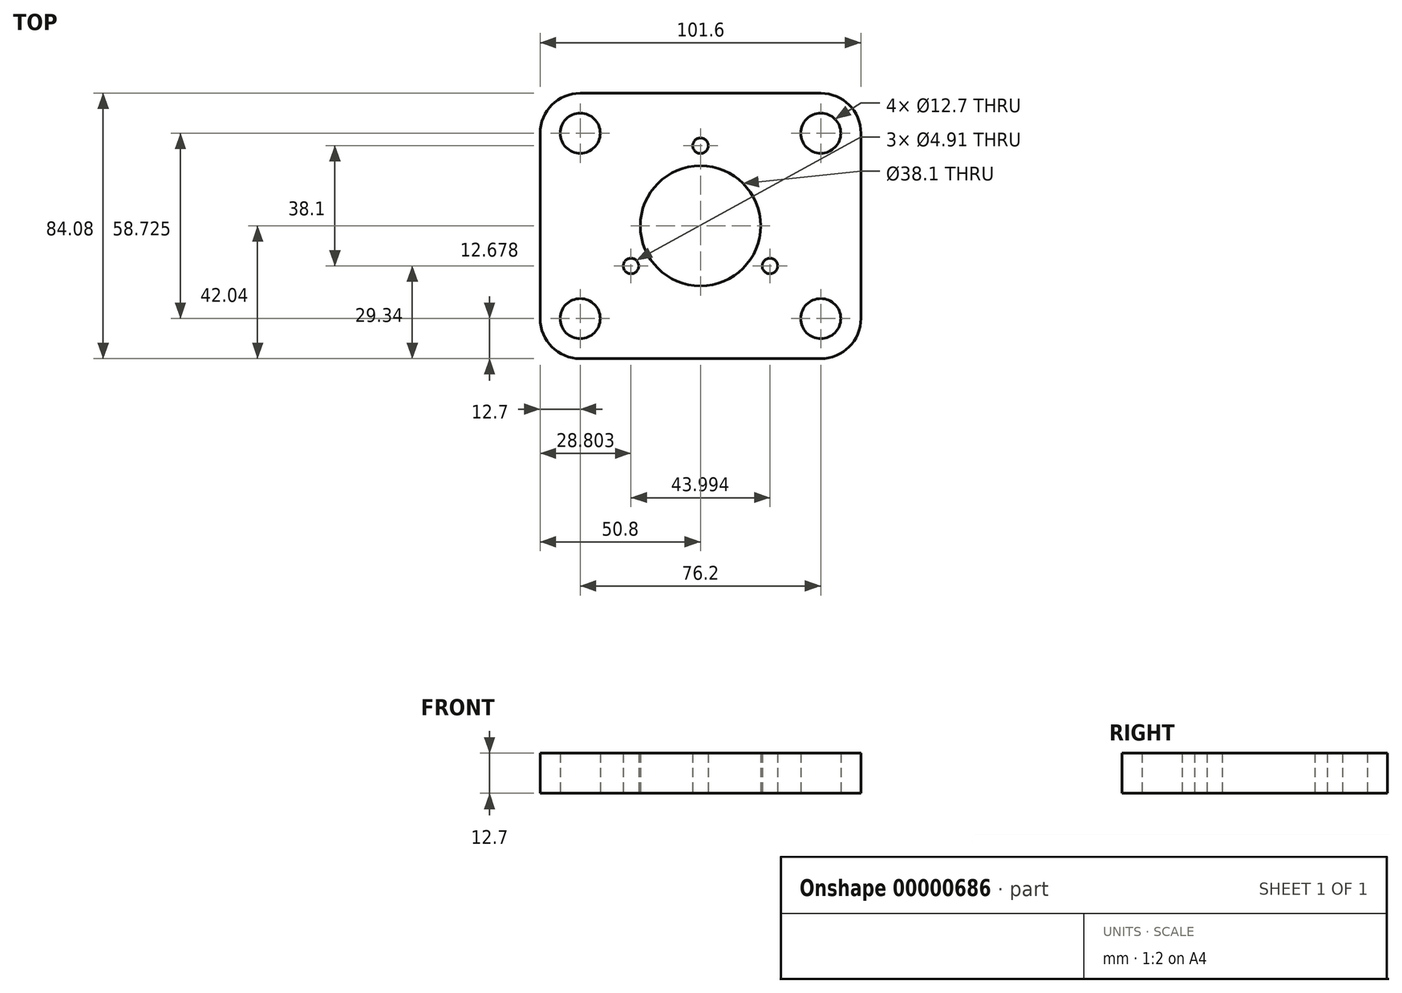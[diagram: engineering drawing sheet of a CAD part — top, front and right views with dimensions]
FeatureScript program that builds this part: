
annotation { "Feature Type Name" : "Feature", "Feature Type Description" : "" }
export const myFeature = defineFeature(function(context is Context, id is Id, definition is map)
    precondition{}
    {
        {
            var Q0;
            Q0=qCreatedBy(makeId("Top.planeOp"),FACE);
            var sketch = newSketch(context, id + "F0", { "sketchPlane" : qUnion([Q0])});
            skLineSegment(sketch, "E0.rect.bottom", {"start": v(-38.1, -42.04) * mm, "end": v(38.1, -42.04) * mm});
            skLineSegment(sketch, "E0.rect.top", {"start": v(-38.1, 42.04) * mm, "end": v(38.1, 42.04) * mm});
            skLineSegment(sketch, "E0.rect.left", {"start": v(-50.8, -29.34) * mm, "end": v(-50.8, 29.34) * mm});
            skLineSegment(sketch, "E0.rect.right", {"start": v(50.8, -29.34) * mm, "end": v(50.8, 29.34) * mm});
            skPoint(sketch, "E0.rect.middle", {"position": v(0, 0) * mm});
            skCircle(sketch, "E1", {"center": v(0, 0) * mm, "radius": 19.05 * mm});
            skLineSegment(sketch, "E2.rect.bottom", {"start": v(-38.1, -29.36) * mm, "end": v(38.1, -29.36) * mm, "construction": true});
            skLineSegment(sketch, "E2.rect.top", {"start": v(-38.1, 29.36) * mm, "end": v(38.1, 29.36) * mm, "construction": true});
            skLineSegment(sketch, "E2.rect.left", {"start": v(-38.1, -29.36) * mm, "end": v(-38.1, 29.36) * mm, "construction": true});
            skLineSegment(sketch, "E2.rect.right", {"start": v(38.1, -29.36) * mm, "end": v(38.1, 29.36) * mm, "construction": true});
            skCircle(sketch, "E3", {"center": v(-38.1, 29.36) * mm, "radius": 6.35 * mm});
            skCircle(sketch, "E4", {"center": v(38.1, 29.36) * mm, "radius": 6.35 * mm});
            skCircle(sketch, "E5", {"center": v(38.1, -29.36) * mm, "radius": 6.35 * mm});
            skCircle(sketch, "E6", {"center": v(-38.1, -29.36) * mm, "radius": 6.35 * mm});
            skPoint(sketch, "E7.visualSharp", {"position": v(-50.8, 42.04) * mm});
            skArc(sketch, "E7.filletArc", {"start": v(-38.1, 42.04) * mm, "mid": v(-47.08, 38.32) * mm, "end": v(-50.8, 29.34) * mm});
            skPoint(sketch, "E8.visualSharp", {"position": v(50.8, 42.04) * mm});
            skArc(sketch, "E8.filletArc", {"start": v(50.8, 29.34) * mm, "mid": v(47.08, 38.32) * mm, "end": v(38.1, 42.04) * mm});
            skPoint(sketch, "E9.visualSharp", {"position": v(50.8, -42.04) * mm});
            skArc(sketch, "E9.filletArc", {"start": v(38.1, -42.04) * mm, "mid": v(47.08, -38.32) * mm, "end": v(50.8, -29.34) * mm});
            skPoint(sketch, "E10.visualSharp", {"position": v(-50.8, -42.04) * mm});
            skArc(sketch, "E10.filletArc", {"start": v(-50.8, -29.34) * mm, "mid": v(-47.08, -38.32) * mm, "end": v(-38.1, -42.04) * mm});
            skCircle(sketch, "E11", {"center": v(0, 0) * mm, "radius": 25.4 * mm, "construction": true});
            skCircle(sketch, "E12", {"center": v(0, 25.4) * mm, "radius": 2.46 * mm});
            skSolve(sketch);
        }
        {
            var Q0;
            Q0=makeQuery(id+"F0.imprint","IMPRINT",FACE,{"disambiguationData":[TD([[makeQuery(id+"F0.imprint","IMPRINT",EDGE,{"derivedFrom":sQuery(id+"F0.wireOp",EDGE,"E0.rect.bottom")}),1.0]])]});
            extrude(context, id + "F1", {"entities" : qUnion([Q0]), "depth" : 12.7 * mm});
        }
        {
            var Q0;
            Q0=makeQuery(id+"F1.opExtrude","SWEPT_FACE",FACE,{"disambiguationData":[OSD([sQuery(id+"F0.wireOp",EDGE,"E12")])]});
            var Q1;
            Q1=makeQuery(id+"F1.opExtrude","SWEPT_FACE",FACE,{"disambiguationData":[OSD([sQuery(id+"F0.wireOp",EDGE,"E1")])]});
            circularPattern(context, id + "F2", {"faces" : qUnion([Q0]), "axis" : qUnion([Q1]), "angle" : 360 * degree, "instanceCount" : 3, "equalSpace" : true, "patternType" : PatternType.FACE});
        }
    });
